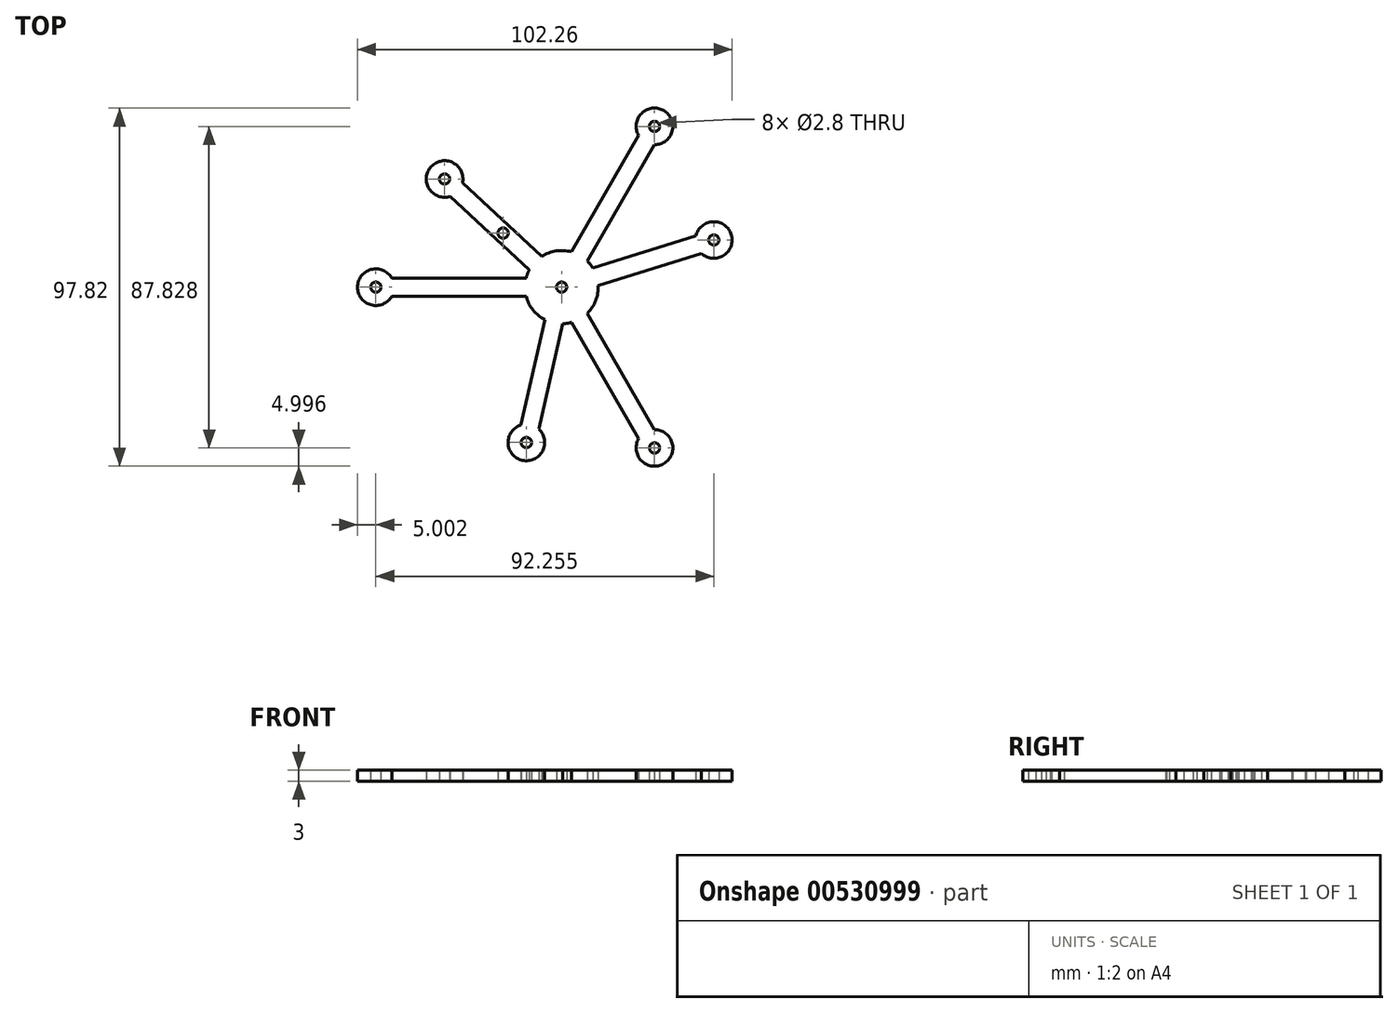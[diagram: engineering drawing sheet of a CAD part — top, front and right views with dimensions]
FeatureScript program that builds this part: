
annotation { "Feature Type Name" : "Feature", "Feature Type Description" : "" }
export const myFeature = defineFeature(function(context is Context, id is Id, definition is map)
    precondition{}
    {
        {
            var Q0;
            Q0=qCreatedBy(makeId("Top.planeOp"),FACE);
            var sketch = newSketch(context, id + "F0", { "sketchPlane" : qUnion([Q0])});
            skLineSegment(sketch, "E0", {"start": v(-50.7, 0) * mm, "end": v(-31.93, 29.54) * mm, "construction": true});
            skPoint(sketch, "E1.center", {"position": v(0, 0) * mm});
            skCircle(sketch, "E2", {"center": v(-50.7, 0) * mm, "radius": 22.5 * mm, "construction": true});
            skCircle(sketch, "E3", {"center": v(0, 0) * mm, "radius": 10 * mm});
            skLineSegment(sketch, "E4", {"start": v(-31.93, 29.54) * mm, "end": v(0, 0) * mm, "construction": true});
            skLineSegment(sketch, "E5", {"start": v(-50.7, 0) * mm, "end": v(0, 0) * mm, "construction": true});
            skCircle(sketch, "E6", {"center": v(-31.93, 29.54) * mm, "radius": 5 * mm});
            skCircle(sketch, "E7", {"center": v(-50.7, 0) * mm, "radius": 5 * mm});
            skLineSegment(sketch, "E8", {"start": v(-30.45, 24.76) * mm, "end": v(-8.8, 4.74) * mm});
            skLineSegment(sketch, "E9", {"start": v(-5.41, 8.41) * mm, "end": v(-27.06, 28.43) * mm});
            skLineSegment(sketch, "E10", {"start": v(-20.17, 15.25) * mm, "end": v(-18.47, 17.08) * mm, "construction": true});
            skLineSegment(sketch, "E11", {"start": v(-18.47, 17.08) * mm, "end": v(-16.77, 18.92) * mm, "construction": true});
            skLineSegment(sketch, "E12", {"start": v(-46.38, 2.5) * mm, "end": v(-9.68, 2.5) * mm});
            skLineSegment(sketch, "E13", {"start": v(-9.68, -2.5) * mm, "end": v(-46.38, -2.5) * mm});
            skLineSegment(sketch, "E14", {"start": v(-29.7, 2.5) * mm, "end": v(-29.7, 0) * mm, "construction": true});
            skLineSegment(sketch, "E15", {"start": v(-29.7, 0) * mm, "end": v(-29.7, -2.5) * mm, "construction": true});
            skCircle(sketch, "E16", {"center": v(-50.7, 0) * mm, "radius": 1.4 * mm});
            skCircle(sketch, "E17", {"center": v(-31.93, 29.54) * mm, "radius": 1.4 * mm});
            skCircle(sketch, "E18", {"center": v(0, 0) * mm, "radius": 1.4 * mm});
            skCircle(sketch, "E19", {"center": v(-31.93, 29.54) * mm, "radius": 12.5 * mm, "construction": true});
            skCircle(sketch, "E20", {"center": v(0, 0) * mm, "radius": 12.5 * mm, "construction": true});
            skCircle(sketch, "E21", {"center": v(-15.97, 14.77) * mm, "radius": 1.4 * mm});
            skCircle(sketch, "E22", {"center": v(-15.97, 14.77) * mm, "radius": 9.25 * mm, "construction": true});
            skLineSegment(sketch, "E23.1.1", {"start": v(-4.58, -8.9) * mm, "end": v(-11.1, -37.65) * mm});
            skLineSegment(sketch, "E23.1.2", {"start": v(-6.22, -38.75) * mm, "end": v(0.3, -10) * mm});
            skCircle(sketch, "E23.1.3", {"center": v(-9.61, -42.42) * mm, "radius": 5 * mm});
            skCircle(sketch, "E23.1.4", {"center": v(-9.61, -42.42) * mm, "radius": 1.4 * mm});
            skCircle(sketch, "E23.1.5", {"center": v(25.35, -43.91) * mm, "radius": 22.5 * mm, "construction": true});
            skCircle(sketch, "E23.1.6", {"center": v(-9.61, -42.42) * mm, "radius": 12.5 * mm, "construction": true});
            skLineSegment(sketch, "E23.1.7", {"start": v(21.02, -41.41) * mm, "end": v(2.68, -9.64) * mm});
            skLineSegment(sketch, "E23.1.8", {"start": v(7, -7.14) * mm, "end": v(25.35, -38.91) * mm});
            skCircle(sketch, "E23.1.9", {"center": v(25.35, -43.91) * mm, "radius": 5 * mm});
            skCircle(sketch, "E23.1.10", {"center": v(25.35, -43.91) * mm, "radius": 1.4 * mm});
            skLineSegment(sketch, "E23.2.1", {"start": v(9.99, 0.48) * mm, "end": v(38.15, 9.22) * mm});
            skLineSegment(sketch, "E23.2.2", {"start": v(36.67, 14) * mm, "end": v(8.5, 5.26) * mm});
            skCircle(sketch, "E23.2.3", {"center": v(41.55, 12.89) * mm, "radius": 5 * mm});
            skCircle(sketch, "E23.2.4", {"center": v(41.55, 12.89) * mm, "radius": 1.4 * mm});
            skCircle(sketch, "E23.2.5", {"center": v(25.35, 43.91) * mm, "radius": 22.5 * mm, "construction": true});
            skCircle(sketch, "E23.2.6", {"center": v(41.55, 12.89) * mm, "radius": 12.5 * mm, "construction": true});
            skLineSegment(sketch, "E23.2.7", {"start": v(25.35, 38.91) * mm, "end": v(7, 7.14) * mm});
            skLineSegment(sketch, "E23.2.8", {"start": v(2.68, 9.64) * mm, "end": v(21.02, 41.41) * mm});
            skCircle(sketch, "E23.2.9", {"center": v(25.35, 43.91) * mm, "radius": 5 * mm});
            skCircle(sketch, "E23.2.10", {"center": v(25.35, 43.91) * mm, "radius": 1.4 * mm});
            skSolve(sketch);
        }
        {
            var Q0;
            Q0 = qSketchRegion(id + "F0", true);
            extrude(context, id + "F1", {"entities" : qUnion([Q0]), "depth" : 3 * mm, "offsetDistance" : 25 * mm});
        }
    });
